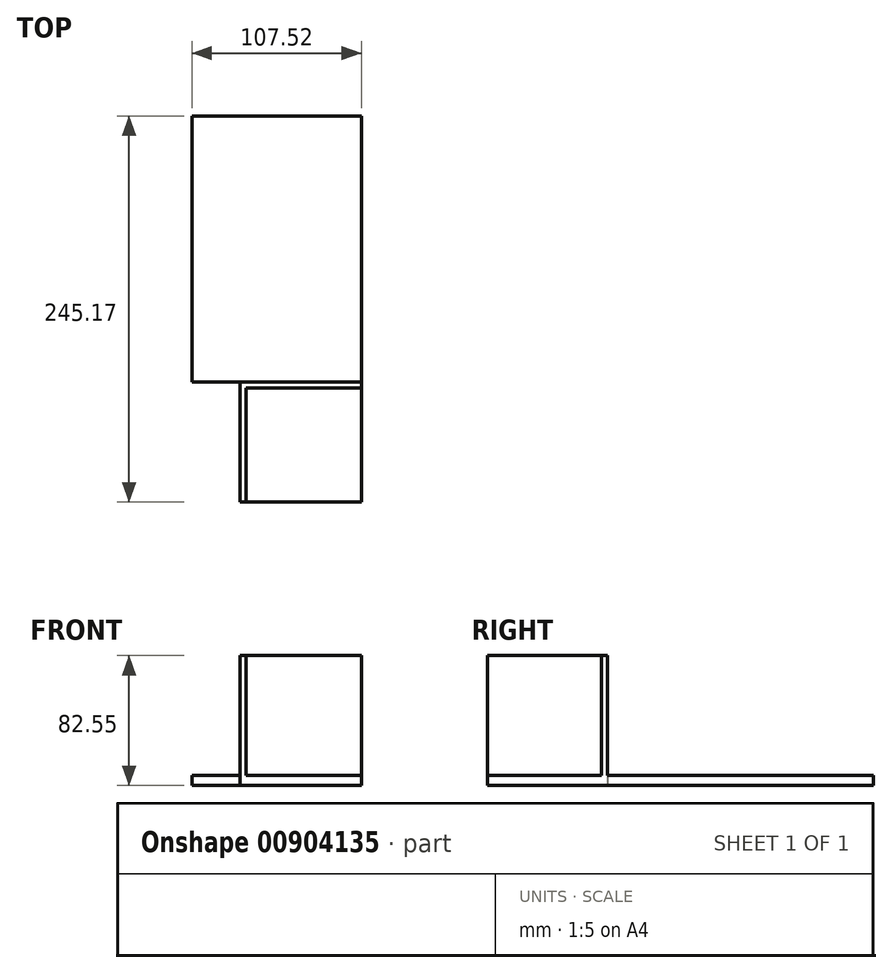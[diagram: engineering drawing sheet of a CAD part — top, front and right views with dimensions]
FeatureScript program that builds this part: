
annotation { "Feature Type Name" : "Feature", "Feature Type Description" : "" }
export const myFeature = defineFeature(function(context is Context, id is Id, definition is map)
    precondition{}
    {
        {
            var Q0;
            Q0=qCreatedBy(makeId("Top.planeOp"),FACE);
            var sketch = newSketch(context, id + "F0", { "sketchPlane" : qUnion([Q0])});
            skLineSegment(sketch, "E0.bottom", {"start": v(0, 0) * mm, "end": v(77.09, 0) * mm});
            skLineSegment(sketch, "E0.top", {"start": v(0, -76.2) * mm, "end": v(77.09, -76.2) * mm});
            skLineSegment(sketch, "E0.left", {"start": v(0, 0) * mm, "end": v(0, -76.2) * mm});
            skLineSegment(sketch, "E0.right", {"start": v(77.09, 0) * mm, "end": v(77.09, -76.2) * mm});
            skSolve(sketch);
        }
        {
            var Q0;
            Q0 = qSketchRegion(id + "F0", true);
            extrude(context, id + "F1", {"entities" : qUnion([Q0]), "depth" : 6.35 * mm, "offsetDistance" : 25.4 * mm});
        }
        {
            var Q0;
            Q0=makeQuery(id+"F1.opExtrude","CAP_FACE",FACE,{"disambiguationData":[OSD([sQuery(id+"F0.wireOp",EDGE,"E0.bottom"),sQuery(id+"F0.wireOp",EDGE,"E0.top"),sQuery(id+"F0.wireOp",EDGE,"E0.left"),sQuery(id+"F0.wireOp",EDGE,"E0.right")])],"isStart":false});
            var sketch = newSketch(context, id + "F2", { "sketchPlane" : qUnion([Q0])});
            skLineSegment(sketch, "E1.bottom", {"start": v(0, -76.2) * mm, "end": v(3.81, -76.2) * mm});
            skLineSegment(sketch, "E1.top", {"start": v(0, 0) * mm, "end": v(3.8, 0) * mm});
            skLineSegment(sketch, "E1.left", {"start": v(0, -76.2) * mm, "end": v(0, 0) * mm});
            skLineSegment(sketch, "E1.right", {"start": v(3.81, -76.2) * mm, "end": v(3.8, 0) * mm});
            skSolve(sketch);
        }
        {
            var Q0;
            Q0 = qSketchRegion(id + "F2", true);
            extrude(context, id + "F3", {"entities" : qUnion([Q0]), "operationType" : NewBodyOperationType.ADD, "depth" : 76.2 * mm, "offsetDistance" : 25.4 * mm});
        }
        {
            var Q0;
            Q0=makeQuery(id+"F1.opExtrude","CAP_FACE",FACE,{"disambiguationData":[OSD([sQuery(id+"F0.wireOp",EDGE,"E0.bottom"),sQuery(id+"F0.wireOp",EDGE,"E0.top"),sQuery(id+"F0.wireOp",EDGE,"E0.left"),sQuery(id+"F0.wireOp",EDGE,"E0.right")])],"isStart":false});
            var sketch = newSketch(context, id + "F4", { "sketchPlane" : qUnion([Q0])});
            skLineSegment(sketch, "E2.bottom", {"start": v(77.09, 0) * mm, "end": v(3.8, 0) * mm});
            skLineSegment(sketch, "E2.top", {"start": v(77.09, -3.81) * mm, "end": v(3.8, -3.81) * mm});
            skLineSegment(sketch, "E2.left", {"start": v(77.09, 0) * mm, "end": v(77.09, -3.81) * mm});
            skLineSegment(sketch, "E2.right", {"start": v(3.8, 0) * mm, "end": v(3.8, -3.81) * mm});
            skSolve(sketch);
        }
        {
            var Q0;
            Q0 = qSketchRegion(id + "F4", true);
            extrude(context, id + "F5", {"entities" : qUnion([Q0]), "operationType" : NewBodyOperationType.ADD, "depth" : 76.2 * mm, "offsetDistance" : 25.4 * mm});
        }
        {
            var Q0;
            Q0=qCreatedBy(makeId("Top.planeOp"),FACE);
            var sketch = newSketch(context, id + "F6", { "sketchPlane" : qUnion([Q0])});
            skPoint(sketch, "E3", {"position": v(77.1, 0) * mm});
            skLineSegment(sketch, "E4.bottom", {"start": v(77.1, 0) * mm, "end": v(-30.42, 0) * mm});
            skLineSegment(sketch, "E4.top", {"start": v(77.1, 168.97) * mm, "end": v(-30.42, 168.97) * mm});
            skLineSegment(sketch, "E4.left", {"start": v(77.1, 0) * mm, "end": v(77.1, 168.97) * mm});
            skLineSegment(sketch, "E4.right", {"start": v(-30.42, 0) * mm, "end": v(-30.42, 168.97) * mm});
            skSolve(sketch);
        }
        {
            var Q0;
            Q0 = qSketchRegion(id + "F6", true);
            extrude(context, id + "F7", {"entities" : qUnion([Q0]), "operationType" : NewBodyOperationType.ADD, "depth" : 6.35 * mm, "offsetDistance" : 25.4 * mm});
        }
    });
